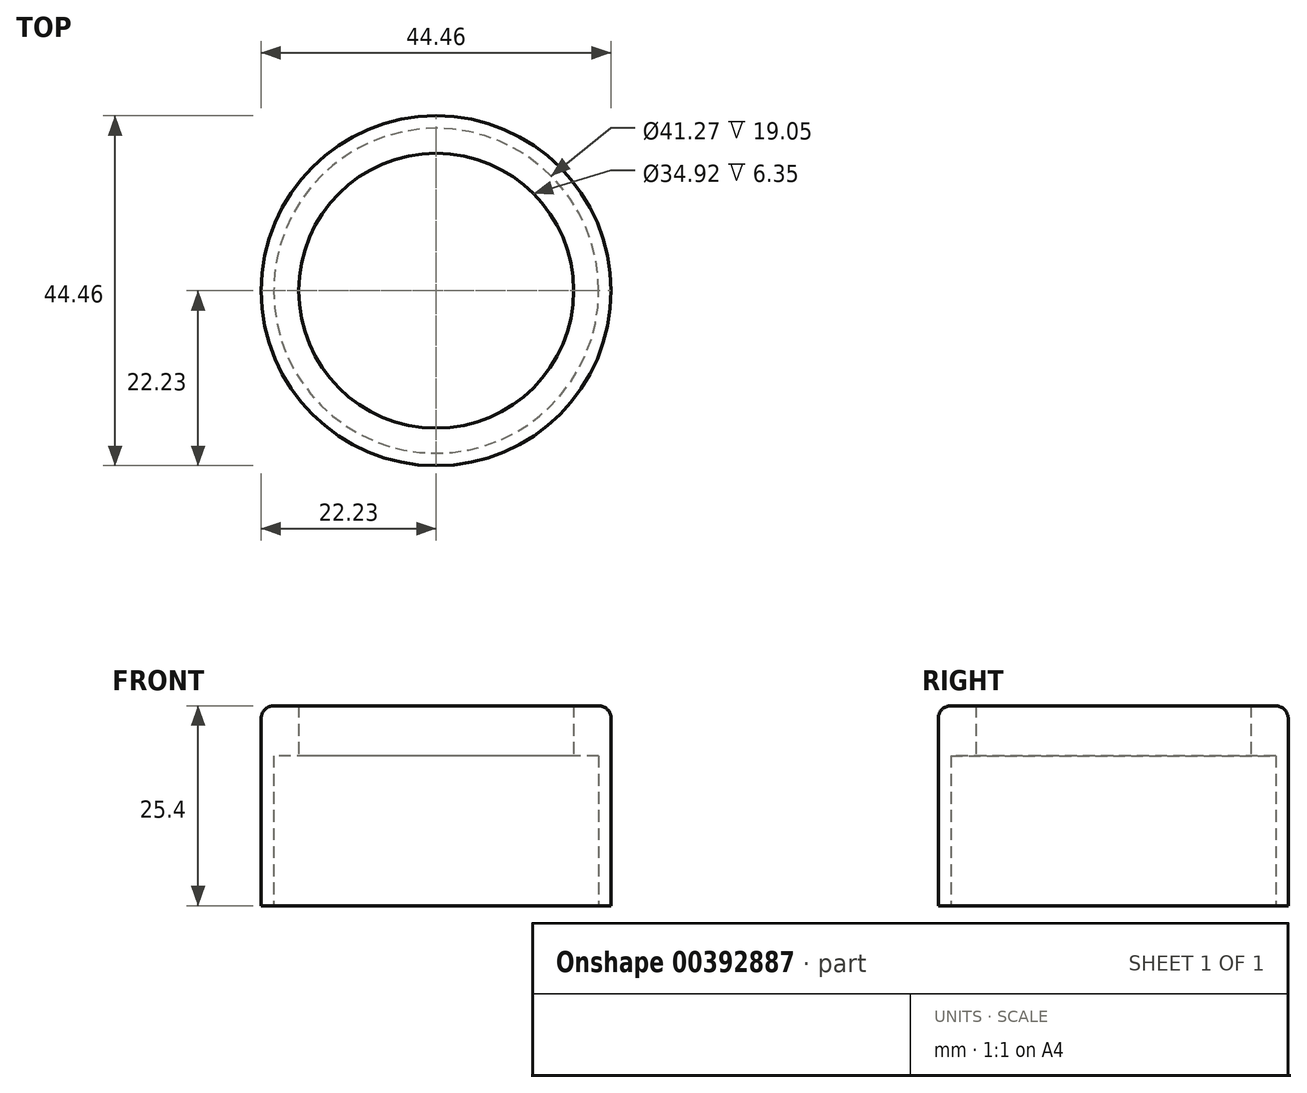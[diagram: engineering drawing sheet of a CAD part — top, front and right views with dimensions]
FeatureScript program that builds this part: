
annotation { "Feature Type Name" : "Feature", "Feature Type Description" : "" }
export const myFeature = defineFeature(function(context is Context, id is Id, definition is map)
    precondition{}
    {
        {
            var Q0;
            Q0=qCreatedBy(makeId("Top.planeOp"),FACE);
            var sketch = newSketch(context, id + "F0", { "sketchPlane" : qUnion([Q0])});
            skCircle(sketch, "E0", {"center": v(0, 0) * mm, "radius": 22.23 * mm});
            skCircle(sketch, "E1", {"center": v(0, 0) * mm, "radius": 20.64 * mm});
            skSolve(sketch);
        }
        {
            var Q0;
            Q0=makeQuery(id+"F0.imprint","IMPRINT",FACE,{"disambiguationData":[TD([[makeQuery(id+"F0.imprint","IMPRINT",EDGE,{"derivedFrom":sQuery(id+"F0.wireOp",EDGE,"E1")}),1.0]])]});
            var Q1;
            Q1=makeQuery(id+"F0.imprint","IMPRINT",FACE,{"disambiguationData":[TD([[makeQuery(id+"F0.imprint","IMPRINT",EDGE,{"derivedFrom":sQuery(id+"F0.wireOp",EDGE,"E0")}),1.0]])]});
            extrude(context, id + "F1", {"entities" : qUnion([Q0, Q1]), "depth" : 25.4 * mm, "offsetDistance" : 25.4 * mm});
        }
        {
            var Q0;
            Q0=makeQuery(id+"F0.imprint","IMPRINT",FACE,{"disambiguationData":[TD([[makeQuery(id+"F0.imprint","IMPRINT",EDGE,{"derivedFrom":sQuery(id+"F0.wireOp",EDGE,"E1")}),1.0]])]});
            extrude(context, id + "F2", {"entities" : qUnion([Q0]), "operationType" : NewBodyOperationType.REMOVE, "depth" : 19.05 * mm, "offsetDistance" : 25.4 * mm});
        }
        {
            var Q0;
            Q0=makeQuery(id+"F1.opExtrude","CAP_FACE",FACE,{"disambiguationData":[OSD([sQuery(id+"F0.wireOp",EDGE,"E0")])],"isStart":false});
            var sketch = newSketch(context, id + "F3", { "sketchPlane" : qUnion([Q0])});
            skPoint(sketch, "E2", {"position": v(0, 0) * mm});
            skSolve(sketch);
        }
        {
            var Q0;
            Q0=sQuery(id+"F3.wireOp",VERTEX,"E2");
            var Q1;
            Q1=makeQuery(id+"F1.opExtrude","SWEPT_BODY",BODY,{"disambiguationData":[OSD([sQuery(id+"F0.wireOp",EDGE,"E0")])]});
            hole(context, id + "F4", {"style" : HoleStyle.SIMPLE, "endStyle" : HoleEndStyle.THROUGH, "holeDiameter" : 34.92 * mm, "majorDiameter" : 6.35 * mm, "isTappedThrough" : true, "tappedDepth" : 12.7 * mm, "tapClearance" : 3, "locations" : qUnion([Q0]), "scope" : qUnion([Q1]), "startStyle" : HoleStartStyle.PART});
        }
        {
            var Q0;
            Q0=makeQuery(id+"F1.opExtrude","CAP_EDGE",EDGE,{"disambiguationData":[OSD([sQuery(id+"F0.wireOp",EDGE,"E0")])],"isStart":false});
            fillet(context, id + "F5", {"entities" : qUnion([Q0]), "radius" : 1.6 * mm, "tangentPropagation" : true, "allowEdgeOverflow" : false});
        }
    });
